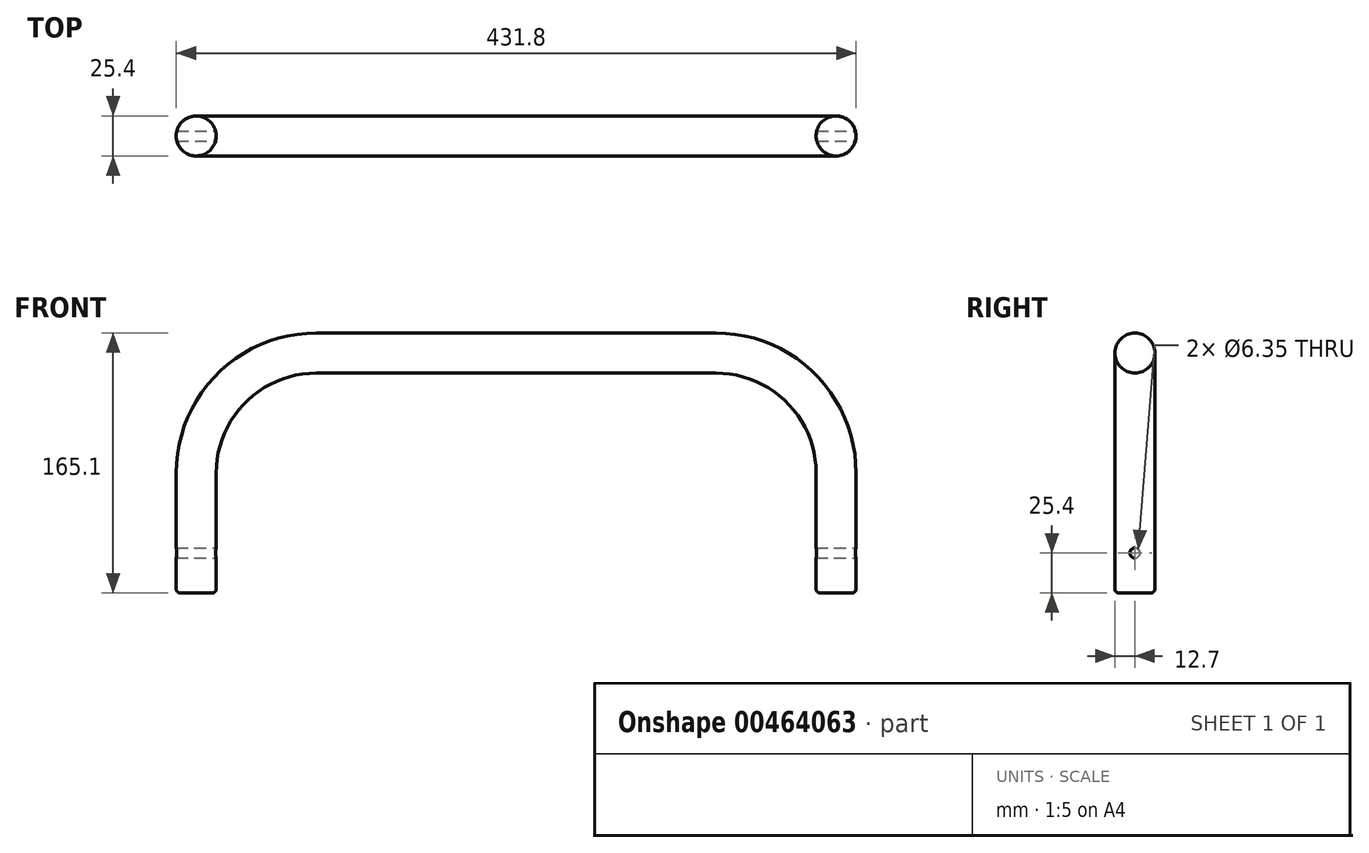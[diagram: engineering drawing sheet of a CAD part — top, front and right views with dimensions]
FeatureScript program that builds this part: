
annotation { "Feature Type Name" : "Feature", "Feature Type Description" : "" }
export const myFeature = defineFeature(function(context is Context, id is Id, definition is map)
    precondition{}
    {
        {
            var Q0;
            Q0=qCreatedBy(makeId("Front.planeOp"),FACE);
            var sketch = newSketch(context, id + "F0", { "sketchPlane" : qUnion([Q0])});
            skLineSegment(sketch, "E0", {"start": v(0, 0) * mm, "end": v(203.2, 0) * mm});
            skLineSegment(sketch, "E1", {"start": v(203.2, 0) * mm, "end": v(203.2, 76.2) * mm});
            skLineSegment(sketch, "E2", {"start": v(0, 0) * mm, "end": v(0, 152.4) * mm});
            skLineSegment(sketch, "E3", {"start": v(0, 152.4) * mm, "end": v(127, 152.4) * mm});
            skArc(sketch, "E4", {"start": v(203.2, 76.2) * mm, "mid": v(180.88, 130.08) * mm, "end": v(127, 152.4) * mm});
            skSolve(sketch);
        }
        {
            var Q0;
            Q0=qCreatedBy(makeId("Top.planeOp"),FACE);
            var sketch = newSketch(context, id + "F1", { "sketchPlane" : qUnion([Q0])});
            skLineSegment(sketch, "E5", {"start": v(0, 0) * mm, "end": v(203.2, 0) * mm});
            skCircle(sketch, "E6", {"center": v(203.2, 0) * mm, "radius": 12.7 * mm});
            skSolve(sketch);
        }
        {
            var Q0;
            Q0=makeQuery(id+"F1.imprint","IMPRINT",FACE,{"disambiguationData":[TD([[makeQuery(id+"F1.imprint","IMPRINT",EDGE,{"derivedFrom":sQuery(id+"F1.wireOp",EDGE,"E6")}),1.0]])]});
            var Q1;
            Q1=sQuery(id+"F0.wireOp",EDGE,"E1");
            var Q2;
            Q2=sQuery(id+"F0.wireOp",EDGE,"E4");
            var Q3;
            Q3=sQuery(id+"F0.wireOp",EDGE,"E3");
            sweep(context, id + "F2", {"profiles" : qUnion([Q0]), "path" : qUnion([Q1, Q2, Q3])});
        }
        {
            var Q0;
            Q0=makeQuery(id+"F2.opSweep","SWEPT_BODY",BODY,{"disambiguationData":[OSD([sQuery(id+"F0.wireOp",EDGE,"E3"),sQuery(id+"F1.wireOp",EDGE,"E6")])]});
            var Q1;
            Q1=qCreatedBy(makeId("Right.planeOp"),FACE);
            mirror(context, id + "F3", {"operationType" : NewBodyOperationType.ADD, "entities" : qUnion([Q0]), "mirrorPlane" : qUnion([Q1])});
        }
        {
            var Q0;
            Q0=makeQuery(id+"F2.opSweep","CAP_EDGE",EDGE,{"disambiguationData":[OSD([sQuery(id+"F0.wireOp",VERTEX,"E1.start"),sQuery(id+"F1.wireOp",EDGE,"E6")])],"isStart":true});
            var Q1;
            Q1=makeQuery(id+"F3.opPattern","COPY",EDGE,{"derivedFrom":makeQuery(id+"F2.opSweep","CAP_EDGE",EDGE,{"disambiguationData":[OSD([sQuery(id+"F0.wireOp",VERTEX,"E1.start"),sQuery(id+"F1.wireOp",EDGE,"E6")])],"isStart":true}),"instanceName":"1"});
            fillet(context, id + "F4", {"entities" : qUnion([Q0, Q1]), "radius" : 2.54 * mm, "tangentPropagation" : true, "allowEdgeOverflow" : false});
        }
        {
            var Q0;
            Q0=qCreatedBy(makeId("Right.planeOp"),FACE);
            cPlane(context, id + "F5", {"entities" : qUnion([Q0]), "cplaneType" : CPlaneType.OFFSET, "offset" : 215.9 * mm, "width" : 152.4 * mm, "height" : 152.4 * mm});
        }
        {
            var Q0;
            Q0=qCreatedBy(makeId("Right.planeOp"),FACE);
            cPlane(context, id + "F6", {"entities" : qUnion([Q0]), "cplaneType" : CPlaneType.OFFSET, "offset" : 215.9 * mm, "oppositeDirection" : true, "width" : 152.4 * mm, "height" : 152.4 * mm});
        }
        {
            var Q0;
            Q0=qCreatedBy(id+"F5.planeOp",FACE);
            var sketch = newSketch(context, id + "F7", { "sketchPlane" : qUnion([Q0])});
            skLineSegment(sketch, "E7", {"start": v(0, 0) * mm, "end": v(0, 25.4) * mm});
            skCircle(sketch, "E8", {"center": v(0, 25.4) * mm, "radius": 3.18 * mm});
            skSolve(sketch);
        }
        {
            var Q0;
            Q0=makeQuery(id+"F7.imprint","IMPRINT",FACE,{"disambiguationData":[TD([[makeQuery(id+"F7.imprint","IMPRINT",EDGE,{"derivedFrom":sQuery(id+"F7.wireOp",EDGE,"E8")}),1.0]])]});
            extrude(context, id + "F8", {"entities" : qUnion([Q0]), "operationType" : NewBodyOperationType.REMOVE, "oppositeDirection" : true, "depth" : 450.09 * mm});
        }
        {
            var Q0;
            Q0=qCreatedBy(id+"F6.planeOp",FACE);
            var sketch = newSketch(context, id + "F9", { "sketchPlane" : qUnion([Q0])});
            skLineSegment(sketch, "E9", {"start": v(0, 0) * mm, "end": v(0, 25.4) * mm});
            skCircle(sketch, "E10", {"center": v(0, 25.4) * mm, "radius": 3.18 * mm});
            skSolve(sketch);
        }
        {
            var Q0;
            Q0=makeQuery(id+"F9.imprint","IMPRINT",FACE,{"disambiguationData":[TD([[makeQuery(id+"F9.imprint","IMPRINT",EDGE,{"derivedFrom":sQuery(id+"F9.wireOp",EDGE,"E10")}),1.0]])]});
            extrude(context, id + "F10", {"entities" : qUnion([Q0]), "operationType" : NewBodyOperationType.REMOVE, "depth" : 6.35 * mm});
        }
    });
